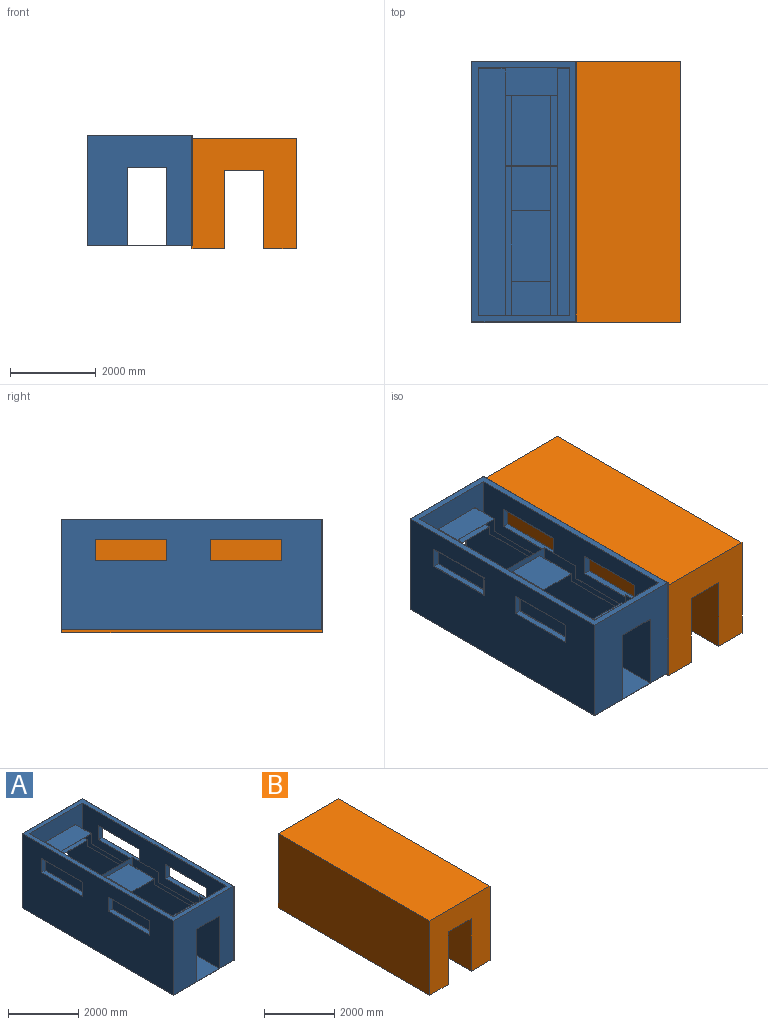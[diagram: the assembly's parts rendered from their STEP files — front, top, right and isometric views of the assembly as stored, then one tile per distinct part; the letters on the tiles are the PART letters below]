
ASSEMBLY  parts=2 mates=1
PART A: 94 faces, bbox 2438.4x6096x2590.8 mm
  f0: plane 639.39x3.05mm, normal (-1,0,0), area 1948.9mm2, adj f6,f9,f27,f55
  f1: plane 800.49x3.05mm, normal (0,0,1), area 2439.9mm2, adj f4,f16,f28,f62
  f2: plane 357.65x3.05mm, normal (0,-1,0), area 1090.1mm2, adj f3,f5,f16,f62
  f3: plane 1652.97x3.05mm, normal (0,0,1), area 5038.3mm2, adj f2,f4,f16,f62
  f4: plane 357.65x3.05mm, normal (0,1,0), area 1090.1mm2, adj f1,f3,f16,f62
  f5: plane 1219.2x1045.38mm, normal (0,0,1), area 6893.1mm2, adj f2,f16,f17,f42,f62,f83
  f6: plane 1219.2x357.65mm, normal (0,-1,0), area 4796.9mm2, adj f0,f7,f9,f16,f55,f62
  f7: plane 1652.97x3.05mm, normal (0,0,1), area 5038.3mm2, adj f6,f16,f42,f62
  f8: plane 914.4x791.79mm, normal (0,0,-1), area 724010.2mm2, adj f12,f13,f23,f41
  f9: plane 1219.2x639.39mm, normal (0,0,1), area 779540.9mm2, adj f0,f6,f16,f27
  f10: plane 6096x2590.8mm, normal (-1,0,0), area 14182814.9mm2, adj f19,f20,f23,f24,f37,f38,f39,f40
  f11: plane 6096x2590.8mm, normal (1,0,0), area 14182814.9mm2, adj f19,f20,f23,f24,f33,f34,f35,f36
  f12: plane 6096x1828.8mm, normal (-1,0,0), area 10469832.3mm2, adj f8,f18,f21,f22,f23,f24,f29,f31
  f13: plane 6096x1828.8mm, normal (1,0,0), area 10469832.3mm2, adj f8,f18,f21,f22,f23,f24,f29,f30
  f14: plane 5791.2x2438.4mm, normal (1,0,0), area 12510560.1mm2, adj f19,f25,f27,f28,f37,f38,f39,f40
  f15: plane 5791.2x2438.4mm, normal (-1,0,0), area 12510560.1mm2, adj f19,f26,f27,f28,f33,f34,f35,f36
  f16: plane 5791.2x1835.97mm, normal (1,0,0), area 9450135.5mm2, adj f1,f2,f3,f4,f5,f6,f7,f9
  f17: plane 357.65x3.05mm, normal (-1,0,0), area 1090.1mm2, adj f5,f42,f83,f84
  f18: plane 1045.38x914.4mm, normal (0,0,-1), area 955893.1mm2, adj f12,f13,f29,f42
  f19: plane 6096x2438.4mm, normal (0,0,1), area 2508382.1mm2, adj f10,f11,f14,f15,f23,f24,f27,f28
  f20: plane 6096x2438.4mm, normal (0,0,-1), area 14864486.4mm2, adj f10,f11,f23,f24
  f21: plane 952.89x914.4mm, normal (0,0,-1), area 871323.8mm2, adj f12,f13,f24,f31
  f22: plane 6096x914.4mm, normal (0,0,1), area 5574182.4mm2, adj f12,f13,f23,f24
  f23: plane 2590.8x2438.4mm, normal (0,1,0), area 4645152mm2, adj f8,f10,f11,f12,f13,f19,f20,f22
  f24: plane 2590.8x2438.4mm, normal (0,-1,0), area 4645152mm2, adj f10,f11,f12,f13,f19,f20,f21,f22
  f25: plane 5791.2x627.93mm, normal (0,0,1), area 3636475.7mm2, adj f14,f27,f28,f63
  f26: plane 5791.2x286.47mm, normal (0,0,1), area 1658997.6mm2, adj f15,f16,f27,f28
  f27: plane 2438.4x2133.6mm, normal (0,-1,0), area 2964150.5mm2, adj f0,f9,f14,f15,f16,f19,f25,f26
  f28: plane 2438.4x2133.6mm, normal (0,1,0), area 2964150.5mm2, adj f1,f14,f15,f16,f19,f25,f26,f53
  f29: plane 920.5x208.29mm, normal (0,-1,0), area 4056.9mm2, adj f12,f13,f18,f30,f32,f58,f59,f64
  f30: plane 1652.97x3.05mm, normal (0,0,1), area 5038.3mm2, adj f13,f29,f31,f59
  f31: plane 920.5x208.29mm, normal (0,1,0), area 4056.9mm2, adj f12,f13,f21,f30,f32,f58,f59,f67
  f32: plane 1652.97x3.05mm, normal (0,0,1), area 5038.3mm2, adj f12,f29,f31,f58
  f33: plane 1652.97x152.4mm, normal (0,0,-1), area 251912.9mm2, adj f11,f15,f34,f36
  f34: plane 487.21x152.4mm, normal (0,-1,0), area 74251.4mm2, adj f11,f15,f33,f35
  f35: plane 1652.97x152.4mm, normal (0,0,1), area 251912.9mm2, adj f11,f15,f34,f36
  f36: plane 487.21x152.4mm, normal (0,1,0), area 74251.4mm2, adj f11,f15,f33,f35
  f37: plane 1652.97x152.4mm, normal (0,0,-1), area 251912.9mm2, adj f10,f14,f38,f40
  f38: plane 487.21x152.4mm, normal (0,1,0), area 74251.4mm2, adj f10,f14,f37,f39
  f39: plane 1652.97x152.4mm, normal (0,0,1), area 251912.9mm2, adj f10,f14,f38,f40
  f40: plane 487.21x152.4mm, normal (0,-1,0), area 74251.4mm2, adj f10,f14,f37,f39
  f41: plane 920.5x208.29mm, normal (0,-1,0), area 4056.9mm2, adj f8,f12,f13,f43,f44,f54,f58,f59
  f42: plane 1219.2x357.65mm, normal (0,1,0), area 248365.1mm2, adj f5,f7,f12,f13,f16,f17,f18,f43
  f43: plane 1652.97x3.05mm, normal (0,0,1), area 5038.3mm2, adj f13,f41,f42,f59
  f44: plane 1652.97x3.05mm, normal (0,0,1), area 5038.3mm2, adj f12,f41,f42,f58
  f45: plane 487.21x152.4mm, normal (0,1,0), area 74251.4mm2, adj f11,f15,f46,f48
  f46: plane 1652.97x152.4mm, normal (0,0,-1), area 251912.9mm2, adj f11,f15,f45,f47
  f47: plane 487.21x152.4mm, normal (0,-1,0), area 74251.4mm2, adj f11,f15,f46,f48
  f48: plane 1652.97x152.4mm, normal (0,0,1), area 251912.9mm2, adj f11,f15,f45,f47
  f49: plane 1652.97x152.4mm, normal (0,0,-1), area 251912.9mm2, adj f10,f14,f51,f52
  f50: plane 1652.97x152.4mm, normal (0,0,1), area 251912.9mm2, adj f10,f14,f51,f52
  f51: plane 487.21x152.4mm, normal (0,-1,0), area 74251.4mm2, adj f10,f14,f49,f50
  f52: plane 487.21x152.4mm, normal (0,1,0), area 74251.4mm2, adj f10,f14,f49,f50
  f53: plane 1216.15x3.05mm, normal (0,0,-1), area 3706.8mm2, adj f28,f62,f63,f74
  f54: plane 920.5x788.74mm, normal (0,0,1), area 726031.3mm2, adj f41,f58,f59,f69
  f55: plane 1216.15x642.44mm, normal (0,0,-1), area 781298.9mm2, adj f0,f6,f62,f63,f73
  f56: plane 6089.9x2584.7mm, normal (1,0,0), area 14103729.8mm2, adj f65,f66,f69,f70,f79,f80,f81,f82
  f57: plane 6089.9x2584.7mm, normal (-1,0,0), area 14103729.8mm2, adj f65,f66,f69,f70,f75,f76,f77,f78
  f58: plane 6089.9x1834.9mm, normal (1,0,0), area 10485096.6mm2, adj f29,f31,f32,f41,f44,f54,f64,f67
  f59: plane 6089.9x1834.9mm, normal (-1,0,0), area 10485096.6mm2, adj f29,f30,f31,f41,f43,f54,f64,f67
  f60: plane 5797.3x2438.4mm, normal (-1,0,0), area 12499257.2mm2, adj f65,f71,f73,f74,f79,f80,f81,f82
  f61: plane 5797.3x2438.4mm, normal (1,0,0), area 12499257.2mm2, adj f65,f72,f73,f74,f75,f76,f77,f78
  f62: plane 5797.3x1839.02mm, normal (-1,0,0), area 9475949.5mm2, adj f1,f2,f3,f4,f5,f6,f7,f53
  f63: plane 5797.3x1839.02mm, normal (1,0,0), area 28853mm2, adj f25,f27,f28,f53,f55,f71,f73,f74
  f64: plane 1042.33x920.5mm, normal (0,0,1), area 959460.1mm2, adj f29,f58,f59,f83
  f65: plane 6089.9x2432.3mm, normal (0,0,-1), area 2408046.8mm2, adj f56,f57,f60,f61,f69,f70,f73,f74
  f66: plane 6089.9x2432.3mm, normal (0,0,1), area 14812497.9mm2, adj f56,f57,f69,f70
  f67: plane 949.84x920.5mm, normal (0,0,1), area 874326.9mm2, adj f31,f58,f59,f70
  f68: plane 6089.9x920.5mm, normal (0,0,-1), area 5605732.3mm2, adj f58,f59,f69,f70
  f69: plane 2584.7x2432.3mm, normal (0,-1,0), area 4597771.4mm2, adj f54,f56,f57,f58,f59,f65,f66,f68
  f70: plane 2584.7x2432.3mm, normal (0,1,0), area 4597771.4mm2, adj f56,f57,f58,f59,f65,f66,f67,f68
  f71: plane 5797.3x630.98mm, normal (0,0,-1), area 3657973.7mm2, adj f60,f63,f73,f74
  f72: plane 5797.3x292.56mm, normal (0,0,-1), area 1696084.2mm2, adj f61,f62,f73,f74
  f73: plane 2438.4x2139.7mm, normal (0,1,0), area 2984611mm2, adj f55,f60,f61,f62,f63,f65,f71,f72
  f74: plane 2438.4x2139.7mm, normal (0,-1,0), area 2980904.2mm2, adj f53,f60,f61,f62,f63,f65,f71,f72
  f75: plane 1659.07x146.3mm, normal (0,0,1), area 242728.3mm2, adj f57,f61,f76,f78
  f76: plane 493.31x146.3mm, normal (0,1,0), area 72173.2mm2, adj f57,f61,f75,f77
  f77: plane 1659.07x146.3mm, normal (0,0,-1), area 242728.3mm2, adj f57,f61,f76,f78
  f78: plane 493.31x146.3mm, normal (0,-1,0), area 72173.2mm2, adj f57,f61,f75,f77
  f79: plane 1659.07x146.3mm, normal (0,0,1), area 242728.3mm2, adj f56,f60,f80,f82
  f80: plane 493.31x146.3mm, normal (0,-1,0), area 72173.2mm2, adj f56,f60,f79,f81
  f81: plane 1659.07x146.3mm, normal (0,0,-1), area 242728.3mm2, adj f56,f60,f80,f82
  f82: plane 493.31x146.3mm, normal (0,1,0), area 72173.2mm2, adj f56,f60,f79,f81
  f83: plane 1216.15x357.65mm, normal (0,-1,0), area 243218.2mm2, adj f5,f17,f58,f59,f62,f64,f84,f85
  f84: plane 149.35x3.05mm, normal (0,0,-1), area 455.2mm2, adj f17,f42,f59,f83
  f85: plane 146.3x3.05mm, normal (0,0,-1), area 445.9mm2, adj f42,f58,f62,f83
  f86: plane 493.31x146.3mm, normal (0,-1,0), area 72173.2mm2, adj f57,f61,f87,f89
  f87: plane 1659.07x146.3mm, normal (0,0,1), area 242728.3mm2, adj f57,f61,f86,f88
  f88: plane 493.31x146.3mm, normal (0,1,0), area 72173.2mm2, adj f57,f61,f87,f89
  f89: plane 1659.07x146.3mm, normal (0,0,-1), area 242728.3mm2, adj f57,f61,f86,f88
  f90: plane 1659.07x146.3mm, normal (0,0,1), area 242728.3mm2, adj f56,f60,f92,f93
  f91: plane 1659.07x146.3mm, normal (0,0,-1), area 242728.3mm2, adj f56,f60,f92,f93
  f92: plane 493.31x146.3mm, normal (0,1,0), area 72173.2mm2, adj f56,f60,f90,f91
  f93: plane 493.31x146.3mm, normal (0,-1,0), area 72173.2mm2, adj f56,f60,f90,f91
PART B: 10 faces, bbox 2438.4x6096x2590.8 mm
  f0: plane 6096x762mm, normal (0,0,-1), area 4645152mm2, adj f1,f2,f6,f9
  f1: plane 2590.8x2438.4mm, normal (0,1,0), area 4645152mm2, adj f0,f2,f3,f4,f5,f7,f8,f9
  f2: plane 6096x2590.8mm, normal (-1,0,0), area 15793516.8mm2, adj f0,f1,f5,f6
  f3: plane 6096x762mm, normal (0,0,-1), area 4645152mm2, adj f1,f4,f6,f7
  f4: plane 6096x2590.8mm, normal (1,0,0), area 15793516.8mm2, adj f1,f3,f5,f6
  f5: plane 6096x2438.4mm, normal (0,0,1), area 14864486.4mm2, adj f1,f2,f4,f6
  f6: plane 2590.8x2438.4mm, normal (0,-1,0), area 4645152mm2, adj f0,f2,f3,f4,f5,f7,f8,f9
  f7: plane 6096x1828.8mm, normal (-1,0,0), area 11148364.8mm2, adj f1,f3,f6,f8
  f8: plane 6096x914.4mm, normal (0,0,-1), area 5574182.4mm2, adj f1,f6,f7,f9
  f9: plane 6096x1828.8mm, normal (1,0,0), area 11148364.8mm2, adj f0,f1,f6,f8
PLACE A t=(-4983.33,-1114.52,-2619.49)mm
PLACE B t=(-2725.93,1924.33,-2690.82)mm
MATE fastened B.f2 <-> A.f11  axis (-1,0,0) through (-3945.13,-1123.67,-2690.82)mm
